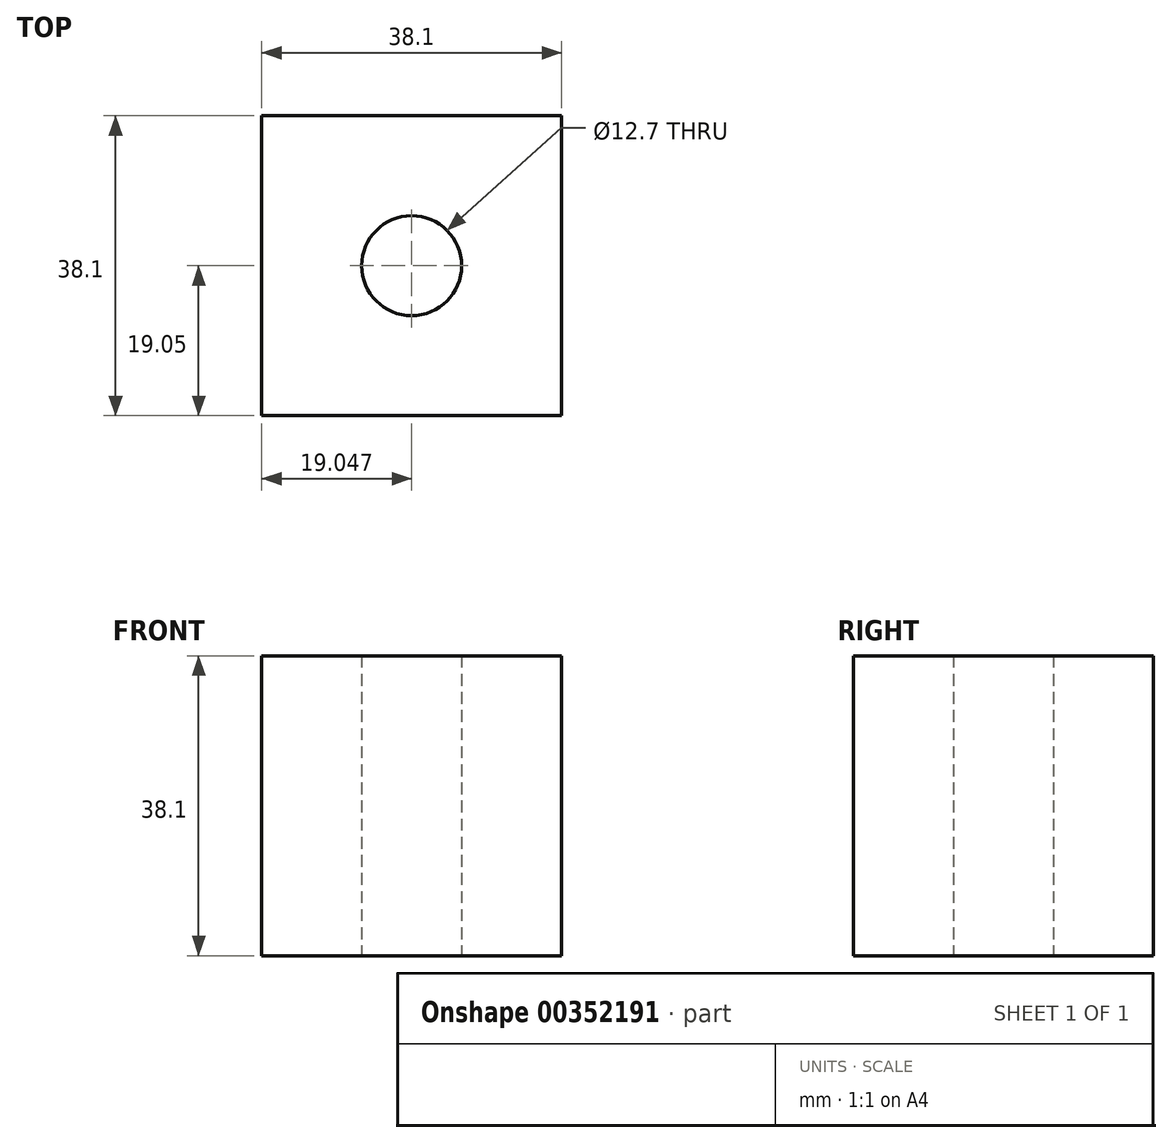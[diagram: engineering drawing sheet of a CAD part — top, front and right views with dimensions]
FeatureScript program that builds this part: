
annotation { "Feature Type Name" : "Feature", "Feature Type Description" : "" }
export const myFeature = defineFeature(function(context is Context, id is Id, definition is map)
    precondition{}
    {
        {
            var Q0;
            Q0=qCreatedBy(makeId("Top.planeOp"),FACE);
            var sketch = newSketch(context, id + "F0", { "sketchPlane" : qUnion([Q0])});
            skLineSegment(sketch, "E0.bottom", {"start": v(0, 0) * mm, "end": v(69.85, 0) * mm});
            skLineSegment(sketch, "E0.top", {"start": v(0, 38.1) * mm, "end": v(69.85, 38.1) * mm});
            skLineSegment(sketch, "E0.left", {"start": v(0, 0) * mm, "end": v(0, 38.1) * mm});
            skArc(sketch, "E1", {"start": v(69.85, 38.1) * mm, "mid": v(88.9, 19.05) * mm, "end": v(69.85, 0) * mm});
            skCircle(sketch, "E2", {"center": v(19.05, 19.05) * mm, "radius": 6.35 * mm});
            skLineSegment(sketch, "E3.bottom", {"start": v(0, 0) * mm, "end": v(38.1, 0) * mm});
            skLineSegment(sketch, "E3.top", {"start": v(0, 38.1) * mm, "end": v(38.1, 38.1) * mm});
            skLineSegment(sketch, "E3.right", {"start": v(38.1, 0) * mm, "end": v(38.1, 38.1) * mm});
            skCircle(sketch, "E4", {"center": v(50.8, 12.7) * mm, "radius": 3.18 * mm});
            skCircle(sketch, "E5", {"center": v(50.8, 25.4) * mm, "radius": 3.18 * mm});
            skCircle(sketch, "E6", {"center": v(69.85, 12.7) * mm, "radius": 3.18 * mm});
            skCircle(sketch, "E7", {"center": v(69.85, 25.4) * mm, "radius": 3.18 * mm});
            skSolve(sketch);
        }
        {
            var Q0;
            Q0=makeQuery(id+"F0.imprint","IMPRINT",FACE,{"disambiguationData":[TD([[makeQuery(id+"F0.imprint","IMPRINT",EDGE,{"derivedFrom":sQuery(id+"F0.wireOp",EDGE,"E0.bottom")}),1.0]])]});
            extrude(context, id + "F1", {"entities" : qUnion([Q0]), "depth" : 12.7 * mm});
        }
        {
            var Q0;
            Q0=makeQuery(id+"F0.imprint","IMPRINT",FACE,{"disambiguationData":[TD([[makeQuery(id+"F0.imprint","IMPRINT",EDGE,{"derivedFrom":sQuery(id+"F0.wireOp",EDGE,"E2")}),-1.0]])]});
            extrude(context, id + "F2", {"entities" : qUnion([Q0]), "operationType" : NewBodyOperationType.ADD, "depth" : 25.4 * mm});
        }
        {
            var Q0;
            Q0=makeQuery(id+"F0.imprint","IMPRINT",FACE,{"disambiguationData":[TD([[makeQuery(id+"F0.imprint","IMPRINT",EDGE,{"derivedFrom":sQuery(id+"F0.wireOp",EDGE,"E2")}),-1.0]])]});
            extrude(context, id + "F3", {"entities" : qUnion([Q0]), "operationType" : NewBodyOperationType.ADD, "oppositeDirection" : true, "depth" : 12.7 * mm});
        }
    });
